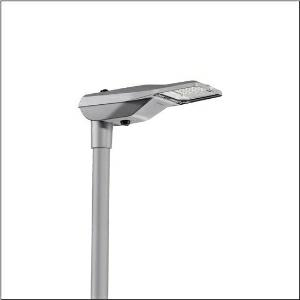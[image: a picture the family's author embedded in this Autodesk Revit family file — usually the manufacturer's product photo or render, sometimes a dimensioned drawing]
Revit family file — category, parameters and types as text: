
# Revit family: streetlight_sl_21_iq_micro___p0_8ab_5xe1r31y08db_c2fe
name_source: partatom
category: Lighting Fixtures
units: mm (PartAtom-declared; Revit-internal decimal feet)

## family parameters
Cut with Voids When Loaded = No
Host = Face
Light Source = No
Part Type = Normal
Room Calculation Point = No
Round Connector Dimension = Use Diameter
Shared = No

## types (1)
- --- (1 x LED, 4550 lm, 39.1 W, 3000K)
    Apparent Load = 39 VA
    CIE Flux Codes = 36 71 98 100 100
    Color Rendering = 70
    Color Temperature = 3000K
    Default Elevation = 1800 mm
    Description = Streetlight SL 21 iQ micro, mast luminaire, primary light control with lens, of PMMA, primary optical cover: cover, of toughened safety glass, transparent, light distribution: P0.8aB, light emission: direct distribution, primary light characteristic: asymmetric, installation type: post-top, side-entry, LED, High Power LED, rated luminous flux: 4.550lm, luminous efficacy: 116lm/W, light colour: 730, colour temperature: 3000K, control gear: iQ-Street Remote, D4i with power reduction, control: pre-setting: logarithmic dimming characteristic, Street-Remote, Auto-Match, Temp-Guard, Lumen-Switch, Night-Set, Smart-Wire, Light-Fading, Desk-Remote (wireless, voltage-free reading and setting of iQ features in the workshop via application-optimized NFC function/RFID function), optimised constant luminous flux control (CLO 2.0), mains connection: 220..240V, AC, 50/60Hz, start of lifetime: 39W, end of service life: 41W, reduction: 17W, luminaire housing, of diecast aluminium, powder-coated, SITECO metallic grey (DB 702S), corrosivity category C5 high according to DIN EN ISO 12944, please order mast flange separately, inclination adjustable: 0°, 5°, 10°, 15°, sealing non-destructively replaceable, multi-level sealing system, length: 528mm, width: 235mm, height: 110mm, mast flange for spigot size: 42mm (side-entry): 5XC10008XM4, 60/48mm (side-entry/post-top): 5XC10108XM2, 76/60mm (side-entry/post-top): 5XC10108XM1, mounting height: 4..8m, Smart Interface below and above, protection rating (complete): IP66, insulation class (complete): insulation class II (safety insulation), certification: CE, ENEC, ENEC+, VDE, impact resistance: IK10, permissible operating ambient temperature for outdoor applications: -40..+50°C, standard-compliant lighting for roads and squares, packaging unit: 1 piece

Light Distribution: P0.8aB
    Height = 110 mm
    Lamp = 1 x LED
    Lamp Light Flux = 4550 lm
    Lamp Power = 39.1 W
    Lamp count = 1
    Length = 528 mm
    Luminous efficacy = 116 lm/W
    Manufacturer = Siteco
    ModVariant = No
    Model = 5XE1R31Y08DB
    Number of Poles = 1
    OnlyDefault = Yes
    Power Factor = 1
    Product Name = Streetlight SL 21 iQ micro | P0.8aB
    Product group = mast luminaire | pylon top
    ProductGroupID = 6100
    Protection Class = Protection class II
    Protection Degree = IP 66
    RLX_Detail_Level = 1
    RLX_Emergency_Light_Flux = 0 lm
    RLX_Emergency_Type = 0
    RLX_Emergency_Type_DB = No
    RlxData = <blob elided: 99201 chars, md5=b1c9196c>
    Socket = socket
    Standby Power = 0 W
    System Light Flux = 4550 lm
    System Power = 39 W
    Type Comments = factory setting: luminous flux: 100 % | dim-lin: 254 | 765 mA
    Type Image = l_1007239.jpg
    URL = http://relux.com
    VarID = @adj_083285
    Voltage = 0 V
    Weight = 0.00 kg
    Width = 235 mm

## geometry (parser evidence)
native form markers: Blend x4, Sweep x10
no freeform markers — native parametric forms only
